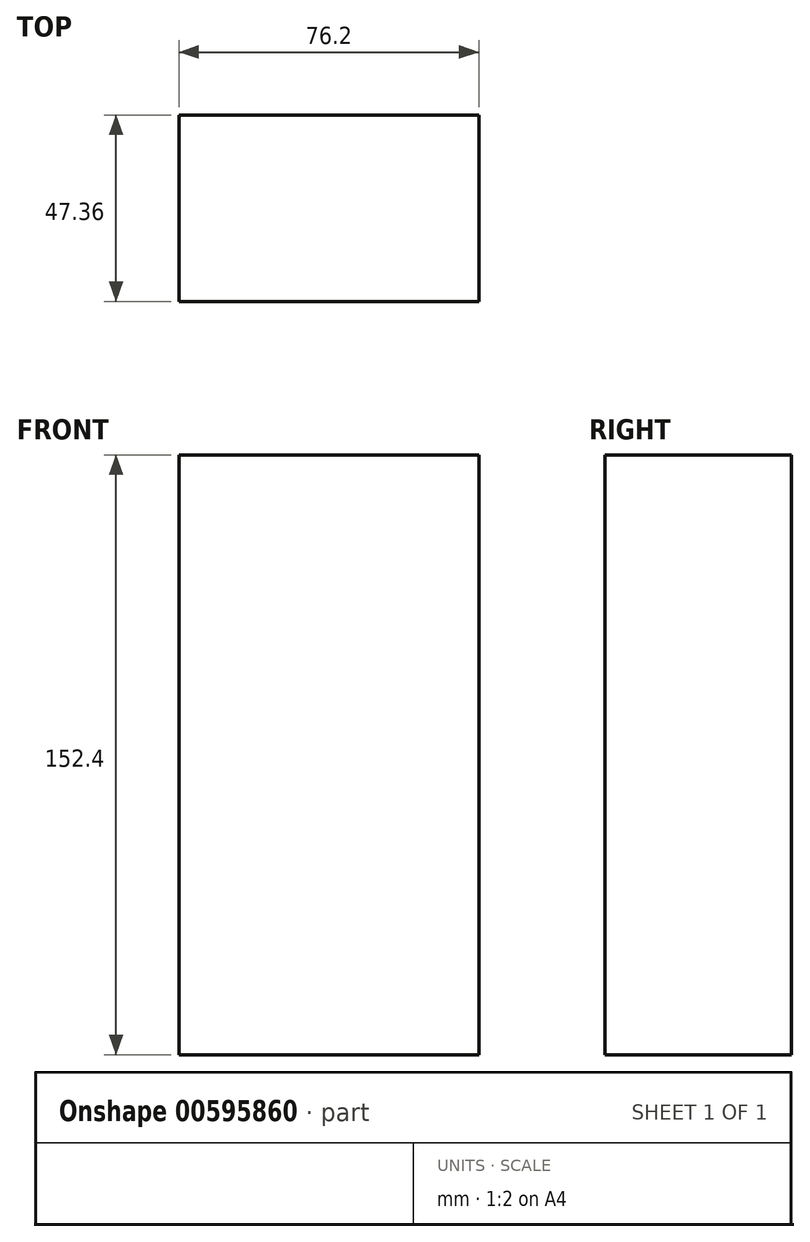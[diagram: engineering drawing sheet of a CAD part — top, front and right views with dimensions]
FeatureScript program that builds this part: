
annotation { "Feature Type Name" : "Feature", "Feature Type Description" : "" }
export const myFeature = defineFeature(function(context is Context, id is Id, definition is map)
    precondition{}
    {
        {
            var Q0;
            Q0=qCreatedBy(makeId("Top.planeOp"),FACE);
            var sketch = newSketch(context, id + "F0", { "sketchPlane" : qUnion([Q0])});
            skLineSegment(sketch, "E0.bottom", {"start": v(-22.08, 19.68) * mm, "end": v(54.12, 19.68) * mm});
            skLineSegment(sketch, "E0.top", {"start": v(-22.08, -27.68) * mm, "end": v(54.12, -27.68) * mm});
            skLineSegment(sketch, "E0.left", {"start": v(-22.08, 19.68) * mm, "end": v(-22.08, -27.68) * mm});
            skLineSegment(sketch, "E0.right", {"start": v(54.12, 19.68) * mm, "end": v(54.12, -27.68) * mm});
            skSolve(sketch);
        }
        {
            var Q0;
            Q0 = qSketchRegion(id + "F0", true);
            extrude(context, id + "F1", {"entities" : qUnion([Q0]), "depth" : 152.4 * mm, "offsetDistance" : 25.4 * mm});
        }
    });
